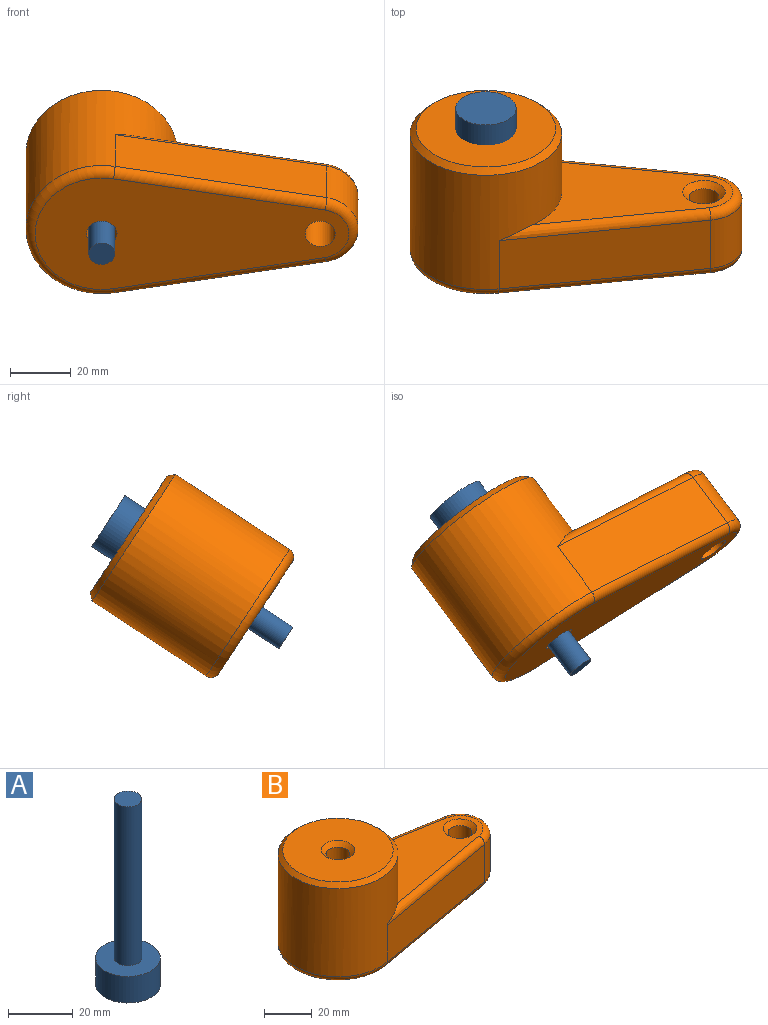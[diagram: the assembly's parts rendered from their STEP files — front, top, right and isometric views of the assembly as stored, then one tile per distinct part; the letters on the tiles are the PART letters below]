
ASSEMBLY  parts=2 mates=1
PART A: 5 faces, bbox 20x20x70 mm
  f0: plane 20x20mm, normal (0,0,1), area 257.4mm2, adj f1,f4
  f1: cylinder r=4.25mm len=60mm, axis (0,0,-1), area 1602.2mm2, adj f0,f2
  f2: plane 8.5x8.5mm, normal (0,0,1), area 56.7mm2, adj f1
  f3: plane 20x20mm, normal (0,0,-1), area 314.2mm2, adj f4
  f4: cylinder r=10mm len=20mm, axis (0,0,-1), area 628.3mm2, adj f0,f3
PART B: 19 faces, bbox 112.5x54.1x50 mm
  f0: cylinder r=25mm len=50mm, axis (0,0,-1), area 5561.6mm2, adj f1,f3,f6,f11,f13,f16,f18
  f1: plane 69.78x19mm, normal (0.17,-0.98,0), area 1346.2mm2, adj f0,f2,f12,f16
  f2: cylinder r=12.5mm len=24.62mm, axis (0,0,-1), area 663.2mm2, adj f1,f3,f14,f17
  f3: plane 69.78x19mm, normal (0.17,0.98,0), area 1346.2mm2, adj f0,f2,f15,f18
  f4: cylinder r=5mm len=48mm, axis (0,0,-1), area 1508mm2, adj f7,f10
  f5: cylinder r=5mm len=23mm, axis (0,0,-1), area 722.6mm2, adj f7,f9
  f6: plane 65.93x39.2mm, normal (0,0,1), area 1379.4mm2, adj f0,f9,f16,f17,f18
  f7: plane 103.45x44mm, normal (0,0,-1), area 3045.6mm2, adj f4,f5,f12,f13,f14,f15
  f8: plane 46x46mm, normal (0,0,1), area 1508mm2, adj f10,f11
  f9: cone r=5mm half-angle=45deg, axis (0,0,1), area 106.6mm2, adj f5,f6
  f10: cone r=5mm half-angle=45deg, axis (0,0,1), area 106.6mm2, adj f4,f8
  f11: cone r=23mm half-angle=45deg, axis (0,0,-1), area 426.5mm2, adj f0,f8
  f12: cylinder r=3mm len=70.3mm, axis (0.98,0.17,0), area 333.9mm2, adj f1,f7,f13,f14
  f13: torus R=22mm, axis (0,0,1), area 393.3mm2, adj f0,f7,f12,f15
  f14: torus R=9.5mm, axis (0,0,1), area 150.1mm2, adj f2,f7,f12,f15
  f15: cylinder r=3mm len=70.3mm, axis (-0.98,0.17,0), area 333.9mm2, adj f3,f7,f13,f14
  f16: cylinder r=3mm len=70.3mm, axis (-0.98,-0.17,0), area 303.9mm2, adj f0,f1,f6,f17
  f17: torus R=9.5mm, axis (0,0,1), area 150.1mm2, adj f2,f6,f16,f18
  f18: cylinder r=3mm len=70.3mm, axis (0.98,-0.17,0), area 303.9mm2, adj f0,f3,f6,f17
PLACE A rot(axis=(0,0.88,-0.47),180deg) t=(-0.7,142.04,-60.06)mm
PLACE B rot(axis=(-1,0,0),56.6deg) t=(-0.7,93.59,-91.94)mm
MATE revolute A.f1 <-> B.f0  axis (0,-0.84,-0.55) through (-0.7,133.69,-65.55)mm
